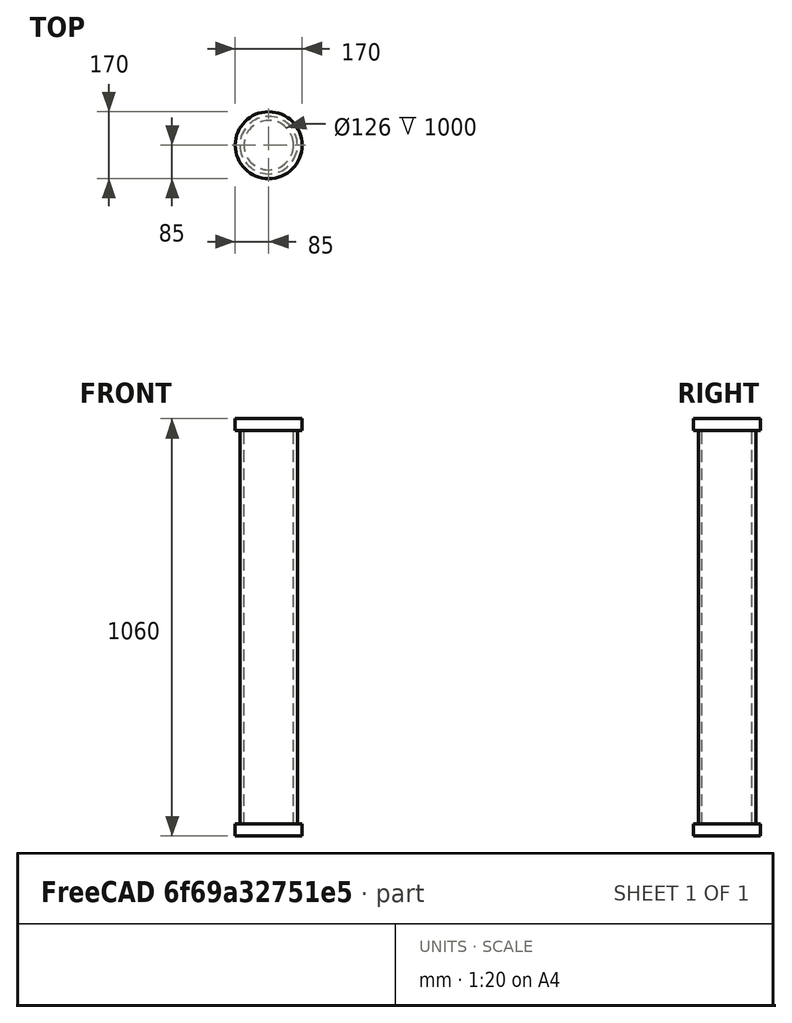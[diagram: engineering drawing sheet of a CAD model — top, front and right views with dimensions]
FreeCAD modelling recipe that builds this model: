
FCSTD DOCUMENT  (FreeCAD 0.19R)
Label: model
License: All rights reserved
LicenseURL: http://en.wikipedia.org/wiki/All_rights_reserved
objects: Mesh::Feature×3, Part::Cylinder×2, Part::FeaturePython×1
note: 3 computed .brp shape members not serialized (recipe doc carries the construction recipe); baked Part::Feature solids carry a one-line shape summary decoded from their .brp

FEATURE [Part::FeaturePython] Tube  # WARN: FeaturePython — macro-defined, semantics opaque (R4)
  AttacherType = Attacher::AttachEngine3D
  Height = 1000
  InnerRadius = 63
  OuterRadius = 73
FEATURE [Part::Cylinder] Cylinder001
  Angle = 360
  AttacherType = Attacher::AttachEngine3D
  Height = 30
  Placement = pos=(0,0,-30) rot=(0,0,1;0rad)
  Radius = 85
FEATURE [Part::Cylinder] Cylinder003
  Angle = 360
  AttacherType = Attacher::AttachEngine3D
  Height = 30
  Placement = pos=(0,0,1000) rot=(0,0,1;0rad)
  Radius = 85
FEATURE [Mesh::Feature] Mesh  label="Tube (Meshed)"
FEATURE [Mesh::Feature] Mesh001  label="Cylinder001 (Meshed)"
FEATURE [Mesh::Feature] Mesh002  label="Cylinder003 (Meshed)"
